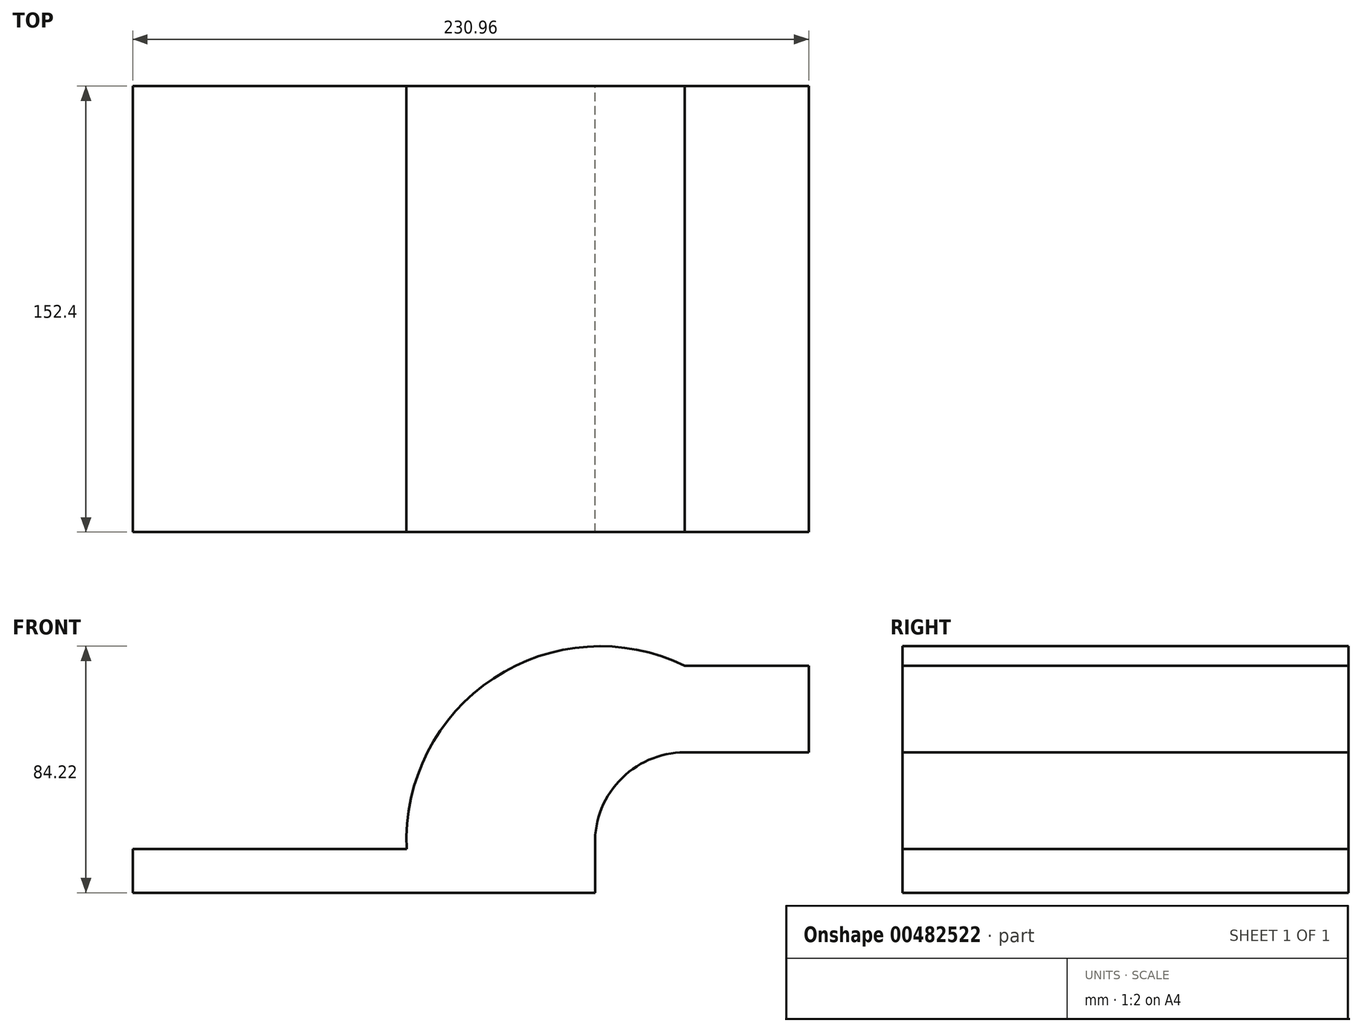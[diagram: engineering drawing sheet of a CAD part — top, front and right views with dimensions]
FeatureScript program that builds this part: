
annotation { "Feature Type Name" : "Feature", "Feature Type Description" : "" }
export const myFeature = defineFeature(function(context is Context, id is Id, definition is map)
    precondition{}
    {
        {
            var Q0;
            Q0=qCreatedBy(makeId("Front.planeOp"),FACE);
            var sketch = newSketch(context, id + "F0", { "sketchPlane" : qUnion([Q0])});
            skLineSegment(sketch, "E0.bottom", {"start": v(-79.01, 7.47) * mm, "end": v(79.01, 7.47) * mm});
            skLineSegment(sketch, "E0.top", {"start": v(-79.01, -7.47) * mm, "end": v(79.01, -7.47) * mm});
            skLineSegment(sketch, "E0.left", {"start": v(-79.01, 7.47) * mm, "end": v(-79.01, -7.47) * mm});
            skLineSegment(sketch, "E0.right", {"start": v(79.01, 7.47) * mm, "end": v(79.01, -7.47) * mm});
            skPoint(sketch, "E0.middle", {"position": v(0, 0) * mm});
            skLineSegment(sketch, "E1.bottom", {"start": v(109.58, 40.46) * mm, "end": v(151.95, 40.46) * mm});
            skLineSegment(sketch, "E1.top", {"start": v(109.58, 70.12) * mm, "end": v(151.95, 70.12) * mm});
            skLineSegment(sketch, "E1.left", {"start": v(109.58, 40.46) * mm, "end": v(109.58, 70.12) * mm});
            skLineSegment(sketch, "E1.right", {"start": v(151.95, 40.46) * mm, "end": v(151.95, 70.12) * mm});
            skPoint(sketch, "E1.middle", {"position": v(130.77, 55.3) * mm});
            skArc(sketch, "E2", {"start": v(109.58, 40.46) * mm, "mid": v(87.1, 30.64) * mm, "end": v(79.01, 7.47) * mm});
            skArc(sketch, "E3", {"start": v(109.58, 70.12) * mm, "mid": v(44.27, 65.81) * mm, "end": v(14.58, 7.47) * mm});
            skSolve(sketch);
        }
        {
            var Q0;
            Q0=makeQuery(id+"F0.imprint","IMPRINT",FACE,{"disambiguationData":[TD([[makeQuery(id+"F0.imprint","IMPRINT",EDGE,{"derivedFrom":sQuery(id+"F0.wireOp",EDGE,"E1.left")}),1.0]])]});
            var Q1;
            Q1=makeQuery(id+"F0.imprint","IMPRINT",FACE,{"disambiguationData":[TD([[makeQuery(id+"F0.imprint","IMPRINT",EDGE,{"derivedFrom":sQuery(id+"F0.wireOp",EDGE,"E0.top")}),1.0]])]});
            var Q2;
            Q2=makeQuery(id+"F0.imprint","IMPRINT",FACE,{"disambiguationData":[TD([[makeQuery(id+"F0.imprint","IMPRINT",EDGE,{"derivedFrom":sQuery(id+"F0.wireOp",EDGE,"E1.bottom")}),1.0]])]});
            extrude(context, id + "F1", {"entities" : qUnion([Q0, Q1, Q2]), "depth" : 152.4 * mm});
        }
    });
